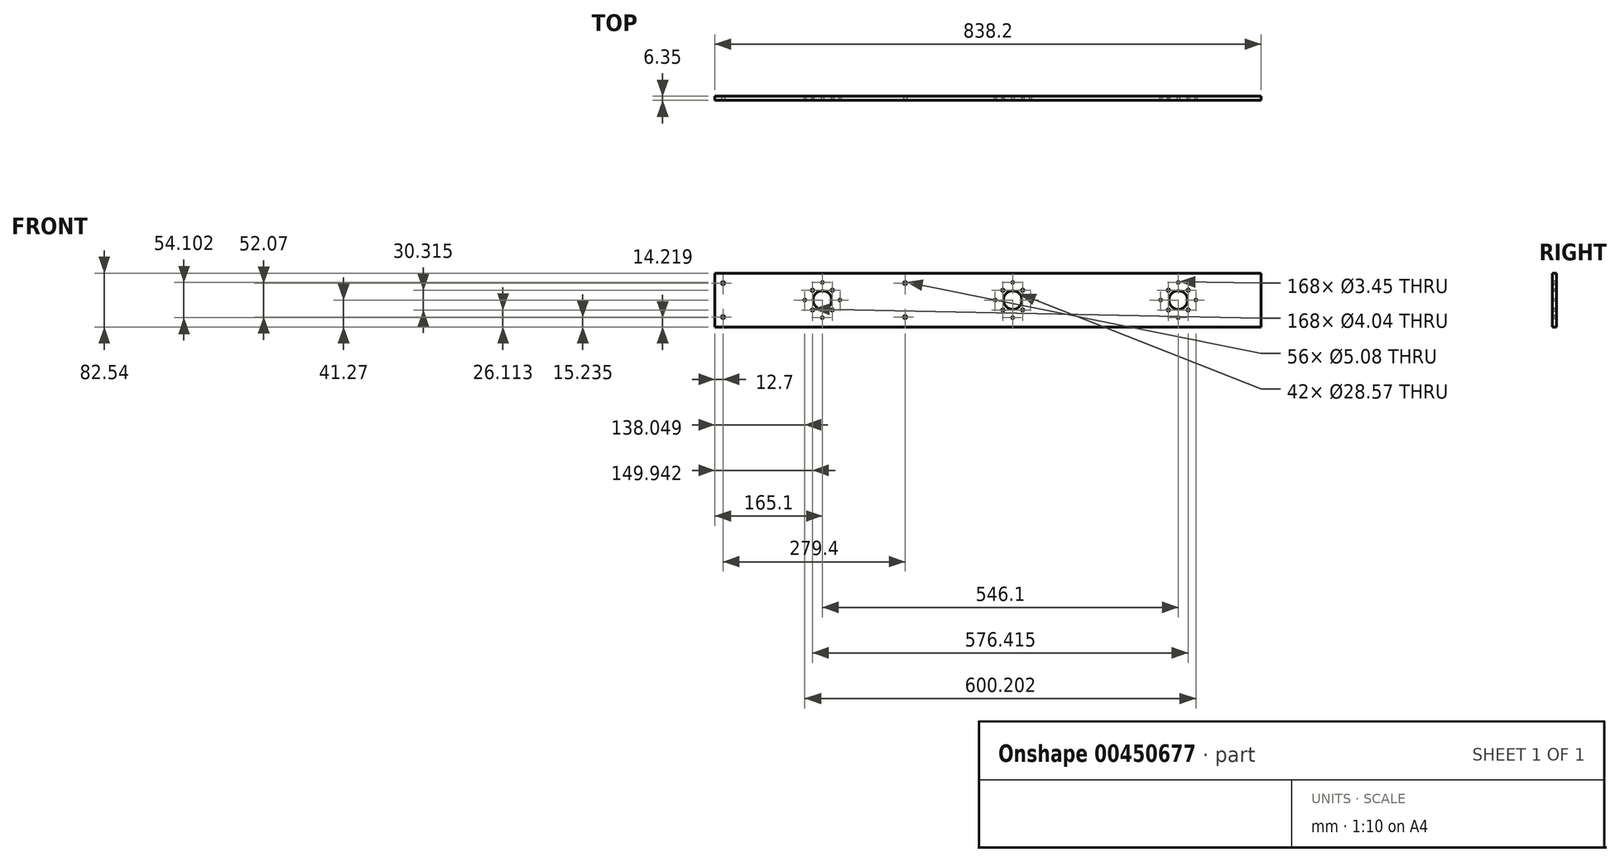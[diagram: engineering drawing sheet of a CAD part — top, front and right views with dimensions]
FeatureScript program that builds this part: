
annotation { "Feature Type Name" : "Feature", "Feature Type Description" : "" }
export const myFeature = defineFeature(function(context is Context, id is Id, definition is map)
    precondition{}
    {
        {
            var Q0;
            Q0=qCreatedBy(makeId("Front.planeOp"),FACE);
            var sketch = newSketch(context, id + "F0", { "sketchPlane" : qUnion([Q0])});
            skLineSegment(sketch, "E0.bottom", {"start": v(419.1, 41.28) * mm, "end": v(-419.1, 41.28) * mm});
            skLineSegment(sketch, "E0.top", {"start": v(419.1, -41.28) * mm, "end": v(-419.1, -41.28) * mm});
            skLineSegment(sketch, "E0.left", {"start": v(419.1, 41.28) * mm, "end": v(419.1, -41.28) * mm});
            skLineSegment(sketch, "E0.right", {"start": v(-419.1, 41.28) * mm, "end": v(-419.1, -41.28) * mm});
            skPoint(sketch, "E0.middle", {"position": v(0, 0) * mm});
            skSolve(sketch);
        }
        {
            var Q0;
            Q0=makeQuery(id+"F0.imprint","IMPRINT",FACE,{"disambiguationData":[TD([[makeQuery(id+"F0.imprint","IMPRINT",EDGE,{"derivedFrom":sQuery(id+"F0.wireOp",EDGE,"E0.bottom")}),1.0]])]});
            extrude(context, id + "F1", {"entities" : qUnion([Q0]), "depth" : 6.35 * mm});
        }
        {
            var Q0;
            Q0=makeQuery(id+"F1.opExtrude","CAP_FACE",FACE,{"disambiguationData":[OSD([sQuery(id+"F0.wireOp",EDGE,"E0.bottom"),sQuery(id+"F0.wireOp",EDGE,"E0.top"),sQuery(id+"F0.wireOp",EDGE,"E0.left"),sQuery(id+"F0.wireOp",EDGE,"E0.right")])],"isStart":false});
            var sketch = newSketch(context, id + "F2", { "sketchPlane" : qUnion([Q0])});
            skLineSegment(sketch, "E1", {"start": v(-419.1, 0) * mm, "end": v(-254, 0) * mm});
            skLineSegment(sketch, "E2", {"start": v(-254, 0) * mm, "end": v(-226.95, 0) * mm});
            skLineSegment(sketch, "E3", {"start": v(-254, 0) * mm, "end": v(-254, 27.05) * mm});
            skLineSegment(sketch, "E4", {"start": v(-254, 0) * mm, "end": v(-254, -27.05) * mm});
            skPoint(sketch, "E5", {"position": v(-281.05, 0) * mm});
            skCircle(sketch, "E6", {"center": v(-254, 27.05) * mm, "radius": 1.73 * mm});
            skCircle(sketch, "E7", {"center": v(-226.95, 0) * mm, "radius": 1.73 * mm});
            skCircle(sketch, "E8", {"center": v(-254, -27.05) * mm, "radius": 1.73 * mm});
            skCircle(sketch, "E9", {"center": v(-281.05, 0) * mm, "radius": 1.73 * mm});
            skCircle(sketch, "E10", {"center": v(-254, 0) * mm, "radius": 14.29 * mm});
            skLineSegment(sketch, "E11", {"start": v(419.1, 0) * mm, "end": v(292.1, 0) * mm});
            skPoint(sketch, "E11.endSnap0", {"position": v(419.1, 0) * mm});
            skPoint(sketch, "E12", {"position": v(319.15, 0) * mm});
            skLineSegment(sketch, "E13", {"start": v(292.1, 0) * mm, "end": v(292.1, 27.05) * mm});
            skLineSegment(sketch, "E14", {"start": v(292.1, 0) * mm, "end": v(292.1, -27.05) * mm});
            skLineSegment(sketch, "E15", {"start": v(292.1, 0) * mm, "end": v(265.05, 0) * mm});
            skCircle(sketch, "E16", {"center": v(292.1, 27.05) * mm, "radius": 1.73 * mm});
            skCircle(sketch, "E17", {"center": v(319.15, 0) * mm, "radius": 1.73 * mm});
            skCircle(sketch, "E18", {"center": v(292.1, -27.05) * mm, "radius": 1.73 * mm});
            skCircle(sketch, "E19", {"center": v(265.05, 0) * mm, "radius": 1.73 * mm});
            skCircle(sketch, "E20", {"center": v(292.1, 0) * mm, "radius": 14.29 * mm});
            skLineSegment(sketch, "E21", {"start": v(38.1, 0) * mm, "end": v(65.15, 0) * mm});
            skLineSegment(sketch, "E22", {"start": v(38.1, 0) * mm, "end": v(38.1, 27.05) * mm});
            skLineSegment(sketch, "E23", {"start": v(38.1, 0) * mm, "end": v(38.1, -27.05) * mm});
            skPoint(sketch, "E24", {"position": v(11.05, 0.16) * mm});
            skCircle(sketch, "E25", {"center": v(38.1, 27.05) * mm, "radius": 1.73 * mm});
            skCircle(sketch, "E26", {"center": v(65.15, 0) * mm, "radius": 1.73 * mm});
            skCircle(sketch, "E27", {"center": v(38.1, -27.05) * mm, "radius": 1.73 * mm});
            skCircle(sketch, "E28", {"center": v(11.05, 0.16) * mm, "radius": 1.73 * mm});
            skCircle(sketch, "E29", {"center": v(38.1, 0) * mm, "radius": 14.29 * mm});
            skLineSegment(sketch, "E30", {"start": v(292.1, 15.16) * mm, "end": v(307.26, 15.16) * mm});
            skLineSegment(sketch, "E31", {"start": v(307.26, 15.16) * mm, "end": v(307.26, -15.16) * mm});
            skLineSegment(sketch, "E32", {"start": v(307.26, -15.16) * mm, "end": v(276.94, -15.16) * mm});
            skLineSegment(sketch, "E33", {"start": v(276.94, -15.16) * mm, "end": v(276.94, 15.16) * mm});
            skLineSegment(sketch, "E34", {"start": v(276.94, 15.16) * mm, "end": v(307.26, 15.16) * mm});
            skCircle(sketch, "E35", {"center": v(276.94, 15.16) * mm, "radius": 2.02 * mm});
            skCircle(sketch, "E36", {"center": v(307.26, 15.16) * mm, "radius": 2.02 * mm});
            skCircle(sketch, "E37", {"center": v(307.26, -15.16) * mm, "radius": 2.02 * mm});
            skCircle(sketch, "E38", {"center": v(276.94, -15.16) * mm, "radius": 2.02 * mm});
            skLineSegment(sketch, "E39", {"start": v(53.26, 15.16) * mm, "end": v(53.26, -15.16) * mm});
            skLineSegment(sketch, "E40", {"start": v(53.26, -15.16) * mm, "end": v(22.94, -15.16) * mm});
            skLineSegment(sketch, "E41", {"start": v(22.94, -15.16) * mm, "end": v(22.94, 15.16) * mm});
            skLineSegment(sketch, "E42", {"start": v(22.94, 15.16) * mm, "end": v(53.26, 15.16) * mm});
            skCircle(sketch, "E43", {"center": v(22.94, 15.16) * mm, "radius": 2.02 * mm});
            skCircle(sketch, "E44", {"center": v(53.26, 15.16) * mm, "radius": 2.02 * mm});
            skCircle(sketch, "E45", {"center": v(53.26, -15.16) * mm, "radius": 2.02 * mm});
            skCircle(sketch, "E46", {"center": v(22.94, -15.16) * mm, "radius": 2.02 * mm});
            skLineSegment(sketch, "E47", {"start": v(53.26, 0) * mm, "end": v(22.94, 0) * mm});
            skLineSegment(sketch, "E48", {"start": v(-238.84, 15.16) * mm, "end": v(-238.84, -15.16) * mm});
            skLineSegment(sketch, "E49", {"start": v(-238.84, -15.16) * mm, "end": v(-269.16, -15.16) * mm});
            skLineSegment(sketch, "E50", {"start": v(-269.16, -15.16) * mm, "end": v(-269.16, 15.16) * mm});
            skLineSegment(sketch, "E51", {"start": v(-269.16, 15.16) * mm, "end": v(-238.84, 15.16) * mm});
            skCircle(sketch, "E52", {"center": v(-269.16, 15.16) * mm, "radius": 2.02 * mm});
            skCircle(sketch, "E53", {"center": v(-238.84, 15.16) * mm, "radius": 2.02 * mm});
            skCircle(sketch, "E54", {"center": v(-238.84, -15.16) * mm, "radius": 2.02 * mm});
            skCircle(sketch, "E55", {"center": v(-269.16, -15.16) * mm, "radius": 2.02 * mm});
            skLineSegment(sketch, "E56", {"start": v(-269.16, 0) * mm, "end": v(-238.84, 0) * mm});
            skLineSegment(sketch, "E57", {"start": v(0, 41.28) * mm, "end": v(38.1, 41.28) * mm});
            skLineSegment(sketch, "E58", {"start": v(38.1, 41.28) * mm, "end": v(38.1, -41.27) * mm});
            skSolve(sketch);
        }
        {
            var Q0;
            {var subQ1=sQuery(id+"F2.wireOp",EDGE,"E4");var subQ3=sQuery(id+"F2.wireOp",EDGE,"E10");var subQ4=makeQuery(id+"F2.imprint","INTERSECT",VERTEX,{"derivedFrom":[subQ1,subQ3]});Q0=makeQuery(id+"F2.imprint","IMPRINT",FACE,{"disambiguationData":[TD([[makeQuery(id+"F2.imprint","IMPRINT",EDGE,{"disambiguationData":[TD([[subQ4,-1.0]])],"derivedFrom":subQ3}),1.0]])]});}
            var Q1;
            {var subQ1=sQuery(id+"F2.wireOp",EDGE,"E3");var subQ3=sQuery(id+"F2.wireOp",EDGE,"E10");var subQ4=makeQuery(id+"F2.imprint","INTERSECT",VERTEX,{"derivedFrom":[subQ1,subQ3]});Q1=makeQuery(id+"F2.imprint","IMPRINT",FACE,{"disambiguationData":[TD([[makeQuery(id+"F2.imprint","IMPRINT",EDGE,{"disambiguationData":[TD([[subQ4,1.0]])],"derivedFrom":subQ3}),1.0]])]});}
            var Q2;
            {var subQ1=sQuery(id+"F2.wireOp",EDGE,"E3");var subQ3=sQuery(id+"F2.wireOp",EDGE,"E10");var subQ4=makeQuery(id+"F2.imprint","INTERSECT",VERTEX,{"derivedFrom":[subQ1,subQ3]});Q2=makeQuery(id+"F2.imprint","IMPRINT",FACE,{"disambiguationData":[TD([[makeQuery(id+"F2.imprint","IMPRINT",EDGE,{"disambiguationData":[TD([[subQ4,-1.0]])],"derivedFrom":subQ3}),1.0]])]});}
            var Q3;
            {var subQ1=sQuery(id+"F2.wireOp",EDGE,"E4");var subQ3=sQuery(id+"F2.wireOp",EDGE,"E10");var subQ4=makeQuery(id+"F2.imprint","INTERSECT",VERTEX,{"derivedFrom":[subQ1,subQ3]});Q3=makeQuery(id+"F2.imprint","IMPRINT",FACE,{"disambiguationData":[TD([[makeQuery(id+"F2.imprint","IMPRINT",EDGE,{"disambiguationData":[TD([[subQ4,1.0]])],"derivedFrom":subQ3}),1.0]])]});}
            var Q4;
            {var subQ0=sQuery(id+"F2.wireOp",EDGE,"E50");var subQ1=sQuery(id+"F2.wireOp",EDGE,"E49");var subQ2=makeQuery(id+"F2.imprint","INTERSECT",VERTEX,{"derivedFrom":[subQ1,subQ0]});Q4=makeQuery(id+"F2.imprint","IMPRINT",FACE,{"disambiguationData":[TD([[makeQuery(id+"F2.imprint","IMPRINT",EDGE,{"disambiguationData":[TD([[subQ2,1.0]])],"derivedFrom":subQ1}),1.0]])]});}
            var Q5;
            {var subQ0=sQuery(id+"F2.wireOp",EDGE,"E50");var subQ1=sQuery(id+"F2.wireOp",EDGE,"E49");var subQ2=makeQuery(id+"F2.imprint","INTERSECT",VERTEX,{"derivedFrom":[subQ1,subQ0]});Q5=makeQuery(id+"F2.imprint","IMPRINT",FACE,{"disambiguationData":[TD([[makeQuery(id+"F2.imprint","IMPRINT",EDGE,{"disambiguationData":[TD([[subQ2,1.0]])],"derivedFrom":subQ1}),-1.0]])]});}
            var Q6;
            Q6=makeQuery(id+"F2.imprint","IMPRINT",FACE,{"disambiguationData":[TD([[makeQuery(id+"F2.imprint","IMPRINT",EDGE,{"derivedFrom":sQuery(id+"F2.wireOp",EDGE,"E8")}),1.0]])]});
            var Q7;
            {var subQ0=sQuery(id+"F2.wireOp",EDGE,"E49");var subQ1=sQuery(id+"F2.wireOp",EDGE,"E48");var subQ2=makeQuery(id+"F2.imprint","INTERSECT",VERTEX,{"derivedFrom":[subQ1,subQ0]});Q7=makeQuery(id+"F2.imprint","IMPRINT",FACE,{"disambiguationData":[TD([[makeQuery(id+"F2.imprint","IMPRINT",EDGE,{"disambiguationData":[TD([[subQ2,1.0]])],"derivedFrom":subQ1}),1.0]])]});}
            var Q8;
            {var subQ0=sQuery(id+"F2.wireOp",EDGE,"E49");var subQ1=sQuery(id+"F2.wireOp",EDGE,"E48");var subQ2=makeQuery(id+"F2.imprint","INTERSECT",VERTEX,{"derivedFrom":[subQ1,subQ0]});Q8=makeQuery(id+"F2.imprint","IMPRINT",FACE,{"disambiguationData":[TD([[makeQuery(id+"F2.imprint","IMPRINT",EDGE,{"disambiguationData":[TD([[subQ2,1.0]])],"derivedFrom":subQ1}),-1.0]])]});}
            var Q9;
            {var subQ0=sQuery(id+"F2.wireOp",EDGE,"E51");var subQ1=sQuery(id+"F2.wireOp",EDGE,"E48");var subQ2=makeQuery(id+"F2.imprint","INTERSECT",VERTEX,{"derivedFrom":[subQ1,subQ0]});Q9=makeQuery(id+"F2.imprint","IMPRINT",FACE,{"disambiguationData":[TD([[makeQuery(id+"F2.imprint","IMPRINT",EDGE,{"disambiguationData":[TD([[subQ2,-1.0]])],"derivedFrom":subQ1}),1.0]])]});}
            var Q10;
            {var subQ0=sQuery(id+"F2.wireOp",EDGE,"E51");var subQ1=sQuery(id+"F2.wireOp",EDGE,"E48");var subQ2=makeQuery(id+"F2.imprint","INTERSECT",VERTEX,{"derivedFrom":[subQ1,subQ0]});Q10=makeQuery(id+"F2.imprint","IMPRINT",FACE,{"disambiguationData":[TD([[makeQuery(id+"F2.imprint","IMPRINT",EDGE,{"disambiguationData":[TD([[subQ2,-1.0]])],"derivedFrom":subQ1}),-1.0]])]});}
            var Q11;
            Q11=makeQuery(id+"F2.imprint","IMPRINT",FACE,{"disambiguationData":[TD([[makeQuery(id+"F2.imprint","IMPRINT",EDGE,{"derivedFrom":sQuery(id+"F2.wireOp",EDGE,"E7")}),1.0]])]});
            var Q12;
            Q12=makeQuery(id+"F2.imprint","IMPRINT",FACE,{"disambiguationData":[TD([[makeQuery(id+"F2.imprint","IMPRINT",EDGE,{"derivedFrom":sQuery(id+"F2.wireOp",EDGE,"E6")}),1.0]])]});
            var Q13;
            {var subQ0=sQuery(id+"F2.wireOp",EDGE,"E51");var subQ1=sQuery(id+"F2.wireOp",EDGE,"E50");var subQ2=makeQuery(id+"F2.imprint","INTERSECT",VERTEX,{"derivedFrom":[subQ1,subQ0]});Q13=makeQuery(id+"F2.imprint","IMPRINT",FACE,{"disambiguationData":[TD([[makeQuery(id+"F2.imprint","IMPRINT",EDGE,{"disambiguationData":[TD([[subQ2,1.0]])],"derivedFrom":subQ1}),-1.0]])]});}
            var Q14;
            {var subQ0=sQuery(id+"F2.wireOp",EDGE,"E51");var subQ1=sQuery(id+"F2.wireOp",EDGE,"E50");var subQ2=makeQuery(id+"F2.imprint","INTERSECT",VERTEX,{"derivedFrom":[subQ1,subQ0]});Q14=makeQuery(id+"F2.imprint","IMPRINT",FACE,{"disambiguationData":[TD([[makeQuery(id+"F2.imprint","IMPRINT",EDGE,{"disambiguationData":[TD([[subQ2,1.0]])],"derivedFrom":subQ1}),1.0]])]});}
            var Q15;
            {var subQ0=sQuery(id+"F2.wireOp",EDGE,"E9");var subQ1=sQuery(id+"F2.wireOp",EDGE,"E1");var subQ2=makeQuery(id+"F2.imprint","INTERSECT",VERTEX,{"disambiguationData":[OD(0.0)],"derivedFrom":[subQ1,subQ0]});Q15=makeQuery(id+"F2.imprint","IMPRINT",FACE,{"disambiguationData":[TD([[makeQuery(id+"F2.imprint","IMPRINT",EDGE,{"disambiguationData":[TD([[subQ2,-1.0]])],"derivedFrom":subQ1}),-1.0]])]});}
            var Q16;
            {var subQ0=sQuery(id+"F2.wireOp",EDGE,"E9");var subQ1=sQuery(id+"F2.wireOp",EDGE,"E1");var subQ2=makeQuery(id+"F2.imprint","INTERSECT",VERTEX,{"disambiguationData":[OD(0.0)],"derivedFrom":[subQ1,subQ0]});Q16=makeQuery(id+"F2.imprint","IMPRINT",FACE,{"disambiguationData":[TD([[makeQuery(id+"F2.imprint","IMPRINT",EDGE,{"disambiguationData":[TD([[subQ2,-1.0]])],"derivedFrom":subQ1}),1.0]])]});}
            var Q17;
            {var subQ1=sQuery(id+"F2.wireOp",EDGE,"E23");var subQ3=sQuery(id+"F2.wireOp",EDGE,"E29");var subQ4=makeQuery(id+"F2.imprint","INTERSECT",VERTEX,{"derivedFrom":[subQ1,subQ3]});Q17=makeQuery(id+"F2.imprint","IMPRINT",FACE,{"disambiguationData":[TD([[makeQuery(id+"F2.imprint","IMPRINT",EDGE,{"disambiguationData":[TD([[subQ4,-1.0]])],"derivedFrom":subQ3}),1.0]])]});}
            var Q18;
            {var subQ1=sQuery(id+"F2.wireOp",EDGE,"E23");var subQ3=sQuery(id+"F2.wireOp",EDGE,"E29");var subQ4=makeQuery(id+"F2.imprint","INTERSECT",VERTEX,{"derivedFrom":[subQ1,subQ3]});Q18=makeQuery(id+"F2.imprint","IMPRINT",FACE,{"disambiguationData":[TD([[makeQuery(id+"F2.imprint","IMPRINT",EDGE,{"disambiguationData":[TD([[subQ4,1.0]])],"derivedFrom":subQ3}),1.0]])]});}
            var Q19;
            {var subQ1=sQuery(id+"F2.wireOp",EDGE,"E22");var subQ3=sQuery(id+"F2.wireOp",EDGE,"E29");var subQ4=makeQuery(id+"F2.imprint","INTERSECT",VERTEX,{"derivedFrom":[subQ1,subQ3]});Q19=makeQuery(id+"F2.imprint","IMPRINT",FACE,{"disambiguationData":[TD([[makeQuery(id+"F2.imprint","IMPRINT",EDGE,{"disambiguationData":[TD([[subQ4,-1.0]])],"derivedFrom":subQ3}),1.0]])]});}
            var Q20;
            {var subQ1=sQuery(id+"F2.wireOp",EDGE,"E22");var subQ3=sQuery(id+"F2.wireOp",EDGE,"E29");var subQ4=makeQuery(id+"F2.imprint","INTERSECT",VERTEX,{"derivedFrom":[subQ1,subQ3]});Q20=makeQuery(id+"F2.imprint","IMPRINT",FACE,{"disambiguationData":[TD([[makeQuery(id+"F2.imprint","IMPRINT",EDGE,{"disambiguationData":[TD([[subQ4,1.0]])],"derivedFrom":subQ3}),1.0]])]});}
            var Q21;
            {var subQ0=sQuery(id+"F2.wireOp",EDGE,"E42");var subQ1=sQuery(id+"F2.wireOp",EDGE,"E39");var subQ2=makeQuery(id+"F2.imprint","INTERSECT",VERTEX,{"derivedFrom":[subQ1,subQ0]});Q21=makeQuery(id+"F2.imprint","IMPRINT",FACE,{"disambiguationData":[TD([[makeQuery(id+"F2.imprint","IMPRINT",EDGE,{"disambiguationData":[TD([[subQ2,-1.0]])],"derivedFrom":subQ1}),1.0]])]});}
            var Q22;
            {var subQ0=sQuery(id+"F2.wireOp",EDGE,"E42");var subQ1=sQuery(id+"F2.wireOp",EDGE,"E39");var subQ2=makeQuery(id+"F2.imprint","INTERSECT",VERTEX,{"derivedFrom":[subQ1,subQ0]});Q22=makeQuery(id+"F2.imprint","IMPRINT",FACE,{"disambiguationData":[TD([[makeQuery(id+"F2.imprint","IMPRINT",EDGE,{"disambiguationData":[TD([[subQ2,-1.0]])],"derivedFrom":subQ1}),-1.0]])]});}
            var Q23;
            Q23=makeQuery(id+"F2.imprint","IMPRINT",FACE,{"disambiguationData":[TD([[makeQuery(id+"F2.imprint","IMPRINT",EDGE,{"derivedFrom":sQuery(id+"F2.wireOp",EDGE,"E25")}),1.0]])]});
            var Q24;
            {var subQ0=sQuery(id+"F2.wireOp",EDGE,"E42");var subQ1=sQuery(id+"F2.wireOp",EDGE,"E41");var subQ2=makeQuery(id+"F2.imprint","INTERSECT",VERTEX,{"derivedFrom":[subQ1,subQ0]});Q24=makeQuery(id+"F2.imprint","IMPRINT",FACE,{"disambiguationData":[TD([[makeQuery(id+"F2.imprint","IMPRINT",EDGE,{"disambiguationData":[TD([[subQ2,1.0]])],"derivedFrom":subQ1}),1.0]])]});}
            var Q25;
            {var subQ0=sQuery(id+"F2.wireOp",EDGE,"E42");var subQ1=sQuery(id+"F2.wireOp",EDGE,"E41");var subQ2=makeQuery(id+"F2.imprint","INTERSECT",VERTEX,{"derivedFrom":[subQ1,subQ0]});Q25=makeQuery(id+"F2.imprint","IMPRINT",FACE,{"disambiguationData":[TD([[makeQuery(id+"F2.imprint","IMPRINT",EDGE,{"disambiguationData":[TD([[subQ2,1.0]])],"derivedFrom":subQ1}),-1.0]])]});}
            var Q26;
            {var subQ0=sQuery(id+"F2.wireOp",EDGE,"E41");var subQ1=sQuery(id+"F2.wireOp",EDGE,"E40");var subQ2=makeQuery(id+"F2.imprint","INTERSECT",VERTEX,{"derivedFrom":[subQ1,subQ0]});Q26=makeQuery(id+"F2.imprint","IMPRINT",FACE,{"disambiguationData":[TD([[makeQuery(id+"F2.imprint","IMPRINT",EDGE,{"disambiguationData":[TD([[subQ2,1.0]])],"derivedFrom":subQ1}),1.0]])]});}
            var Q27;
            {var subQ0=sQuery(id+"F2.wireOp",EDGE,"E41");var subQ1=sQuery(id+"F2.wireOp",EDGE,"E40");var subQ2=makeQuery(id+"F2.imprint","INTERSECT",VERTEX,{"derivedFrom":[subQ1,subQ0]});Q27=makeQuery(id+"F2.imprint","IMPRINT",FACE,{"disambiguationData":[TD([[makeQuery(id+"F2.imprint","IMPRINT",EDGE,{"disambiguationData":[TD([[subQ2,1.0]])],"derivedFrom":subQ1}),-1.0]])]});}
            var Q28;
            Q28=makeQuery(id+"F2.imprint","IMPRINT",FACE,{"disambiguationData":[TD([[makeQuery(id+"F2.imprint","IMPRINT",EDGE,{"derivedFrom":sQuery(id+"F2.wireOp",EDGE,"E27")}),1.0]])]});
            var Q29;
            {var subQ0=sQuery(id+"F2.wireOp",EDGE,"E40");var subQ1=sQuery(id+"F2.wireOp",EDGE,"E39");var subQ2=makeQuery(id+"F2.imprint","INTERSECT",VERTEX,{"derivedFrom":[subQ1,subQ0]});Q29=makeQuery(id+"F2.imprint","IMPRINT",FACE,{"disambiguationData":[TD([[makeQuery(id+"F2.imprint","IMPRINT",EDGE,{"disambiguationData":[TD([[subQ2,1.0]])],"derivedFrom":subQ1}),1.0]])]});}
            var Q30;
            {var subQ0=sQuery(id+"F2.wireOp",EDGE,"E40");var subQ1=sQuery(id+"F2.wireOp",EDGE,"E39");var subQ2=makeQuery(id+"F2.imprint","INTERSECT",VERTEX,{"derivedFrom":[subQ1,subQ0]});Q30=makeQuery(id+"F2.imprint","IMPRINT",FACE,{"disambiguationData":[TD([[makeQuery(id+"F2.imprint","IMPRINT",EDGE,{"disambiguationData":[TD([[subQ2,1.0]])],"derivedFrom":subQ1}),-1.0]])]});}
            var Q31;
            Q31=makeQuery(id+"F2.imprint","IMPRINT",FACE,{"disambiguationData":[TD([[makeQuery(id+"F2.imprint","IMPRINT",EDGE,{"derivedFrom":sQuery(id+"F2.wireOp",EDGE,"E28")}),1.0]])]});
            var Q32;
            Q32=makeQuery(id+"F2.imprint","IMPRINT",FACE,{"disambiguationData":[TD([[makeQuery(id+"F2.imprint","IMPRINT",EDGE,{"derivedFrom":sQuery(id+"F2.wireOp",EDGE,"E26")}),1.0]])]});
            var Q33;
            {var subQ1=sQuery(id+"F2.wireOp",EDGE,"E11");var subQ3=sQuery(id+"F2.wireOp",EDGE,"E20");var subQ4=makeQuery(id+"F2.imprint","INTERSECT",VERTEX,{"derivedFrom":[subQ1,subQ3]});Q33=makeQuery(id+"F2.imprint","IMPRINT",FACE,{"disambiguationData":[TD([[makeQuery(id+"F2.imprint","IMPRINT",EDGE,{"disambiguationData":[TD([[subQ4,1.0]])],"derivedFrom":subQ3}),1.0]])]});}
            var Q34;
            {var subQ1=sQuery(id+"F2.wireOp",EDGE,"E11");var subQ3=sQuery(id+"F2.wireOp",EDGE,"E20");var subQ4=makeQuery(id+"F2.imprint","INTERSECT",VERTEX,{"derivedFrom":[subQ1,subQ3]});Q34=makeQuery(id+"F2.imprint","IMPRINT",FACE,{"disambiguationData":[TD([[makeQuery(id+"F2.imprint","IMPRINT",EDGE,{"disambiguationData":[TD([[subQ4,-1.0]])],"derivedFrom":subQ3}),1.0]])]});}
            var Q35;
            {var subQ1=sQuery(id+"F2.wireOp",EDGE,"E13");var subQ3=sQuery(id+"F2.wireOp",EDGE,"E20");var subQ4=makeQuery(id+"F2.imprint","INTERSECT",VERTEX,{"derivedFrom":[subQ1,subQ3]});Q35=makeQuery(id+"F2.imprint","IMPRINT",FACE,{"disambiguationData":[TD([[makeQuery(id+"F2.imprint","IMPRINT",EDGE,{"disambiguationData":[TD([[subQ4,-1.0]])],"derivedFrom":subQ3}),1.0]])]});}
            var Q36;
            {var subQ1=sQuery(id+"F2.wireOp",EDGE,"E14");var subQ3=sQuery(id+"F2.wireOp",EDGE,"E20");var subQ4=makeQuery(id+"F2.imprint","INTERSECT",VERTEX,{"derivedFrom":[subQ1,subQ3]});Q36=makeQuery(id+"F2.imprint","IMPRINT",FACE,{"disambiguationData":[TD([[makeQuery(id+"F2.imprint","IMPRINT",EDGE,{"disambiguationData":[TD([[subQ4,1.0]])],"derivedFrom":subQ3}),1.0]])]});}
            var Q37;
            {var subQ0=sQuery(id+"F2.wireOp",EDGE,"E32");var subQ1=sQuery(id+"F2.wireOp",EDGE,"E31");var subQ2=makeQuery(id+"F2.imprint","INTERSECT",VERTEX,{"derivedFrom":[subQ1,subQ0]});Q37=makeQuery(id+"F2.imprint","IMPRINT",FACE,{"disambiguationData":[TD([[makeQuery(id+"F2.imprint","IMPRINT",EDGE,{"disambiguationData":[TD([[subQ2,1.0]])],"derivedFrom":subQ1}),1.0]])]});}
            var Q38;
            {var subQ0=sQuery(id+"F2.wireOp",EDGE,"E32");var subQ1=sQuery(id+"F2.wireOp",EDGE,"E31");var subQ2=makeQuery(id+"F2.imprint","INTERSECT",VERTEX,{"derivedFrom":[subQ1,subQ0]});Q38=makeQuery(id+"F2.imprint","IMPRINT",FACE,{"disambiguationData":[TD([[makeQuery(id+"F2.imprint","IMPRINT",EDGE,{"disambiguationData":[TD([[subQ2,1.0]])],"derivedFrom":subQ1}),-1.0]])]});}
            var Q39;
            Q39=makeQuery(id+"F2.imprint","IMPRINT",FACE,{"disambiguationData":[TD([[makeQuery(id+"F2.imprint","IMPRINT",EDGE,{"derivedFrom":sQuery(id+"F2.wireOp",EDGE,"E18")}),1.0]])]});
            var Q40;
            {var subQ0=sQuery(id+"F2.wireOp",EDGE,"E17");var subQ1=sQuery(id+"F2.wireOp",EDGE,"E11");var subQ2=makeQuery(id+"F2.imprint","INTERSECT",VERTEX,{"disambiguationData":[OD(0.0)],"derivedFrom":[subQ1,subQ0]});Q40=makeQuery(id+"F2.imprint","IMPRINT",FACE,{"disambiguationData":[TD([[makeQuery(id+"F2.imprint","IMPRINT",EDGE,{"disambiguationData":[TD([[subQ2,1.0]])],"derivedFrom":subQ1}),1.0]])]});}
            var Q41;
            {var subQ0=sQuery(id+"F2.wireOp",EDGE,"E17");var subQ1=sQuery(id+"F2.wireOp",EDGE,"E11");var subQ2=makeQuery(id+"F2.imprint","INTERSECT",VERTEX,{"disambiguationData":[OD(0.0)],"derivedFrom":[subQ1,subQ0]});Q41=makeQuery(id+"F2.imprint","IMPRINT",FACE,{"disambiguationData":[TD([[makeQuery(id+"F2.imprint","IMPRINT",EDGE,{"disambiguationData":[TD([[subQ2,1.0]])],"derivedFrom":subQ1}),-1.0]])]});}
            var Q42;
            {var subQ0=sQuery(id+"F2.wireOp",EDGE,"E34");var subQ1=sQuery(id+"F2.wireOp",EDGE,"E31");var subQ2=makeQuery(id+"F2.imprint","INTERSECT",VERTEX,{"derivedFrom":[subQ1,subQ0]});Q42=makeQuery(id+"F2.imprint","IMPRINT",FACE,{"disambiguationData":[TD([[makeQuery(id+"F2.imprint","IMPRINT",EDGE,{"disambiguationData":[TD([[subQ2,-1.0]])],"derivedFrom":subQ1}),1.0]])]});}
            var Q43;
            {var subQ0=sQuery(id+"F2.wireOp",EDGE,"E34");var subQ1=sQuery(id+"F2.wireOp",EDGE,"E31");var subQ2=makeQuery(id+"F2.imprint","INTERSECT",VERTEX,{"derivedFrom":[subQ1,subQ0]});Q43=makeQuery(id+"F2.imprint","IMPRINT",FACE,{"disambiguationData":[TD([[makeQuery(id+"F2.imprint","IMPRINT",EDGE,{"disambiguationData":[TD([[subQ2,-1.0]])],"derivedFrom":subQ1}),-1.0]])]});}
            var Q44;
            Q44=makeQuery(id+"F2.imprint","IMPRINT",FACE,{"disambiguationData":[TD([[makeQuery(id+"F2.imprint","IMPRINT",EDGE,{"derivedFrom":sQuery(id+"F2.wireOp",EDGE,"E16")}),1.0]])]});
            var Q45;
            {var subQ0=sQuery(id+"F2.wireOp",EDGE,"E34");var subQ1=sQuery(id+"F2.wireOp",EDGE,"E33");var subQ2=makeQuery(id+"F2.imprint","INTERSECT",VERTEX,{"derivedFrom":[subQ1,subQ0]});Q45=makeQuery(id+"F2.imprint","IMPRINT",FACE,{"disambiguationData":[TD([[makeQuery(id+"F2.imprint","IMPRINT",EDGE,{"disambiguationData":[TD([[subQ2,1.0]])],"derivedFrom":subQ1}),-1.0]])]});}
            var Q46;
            {var subQ0=sQuery(id+"F2.wireOp",EDGE,"E34");var subQ1=sQuery(id+"F2.wireOp",EDGE,"E33");var subQ2=makeQuery(id+"F2.imprint","INTERSECT",VERTEX,{"derivedFrom":[subQ1,subQ0]});Q46=makeQuery(id+"F2.imprint","IMPRINT",FACE,{"disambiguationData":[TD([[makeQuery(id+"F2.imprint","IMPRINT",EDGE,{"disambiguationData":[TD([[subQ2,1.0]])],"derivedFrom":subQ1}),1.0]])]});}
            var Q47;
            {var subQ0=sQuery(id+"F2.wireOp",EDGE,"E33");var subQ1=sQuery(id+"F2.wireOp",EDGE,"E32");var subQ2=makeQuery(id+"F2.imprint","INTERSECT",VERTEX,{"derivedFrom":[subQ1,subQ0]});Q47=makeQuery(id+"F2.imprint","IMPRINT",FACE,{"disambiguationData":[TD([[makeQuery(id+"F2.imprint","IMPRINT",EDGE,{"disambiguationData":[TD([[subQ2,1.0]])],"derivedFrom":subQ1}),1.0]])]});}
            var Q48;
            {var subQ0=sQuery(id+"F2.wireOp",EDGE,"E33");var subQ1=sQuery(id+"F2.wireOp",EDGE,"E32");var subQ2=makeQuery(id+"F2.imprint","INTERSECT",VERTEX,{"derivedFrom":[subQ1,subQ0]});Q48=makeQuery(id+"F2.imprint","IMPRINT",FACE,{"disambiguationData":[TD([[makeQuery(id+"F2.imprint","IMPRINT",EDGE,{"disambiguationData":[TD([[subQ2,1.0]])],"derivedFrom":subQ1}),-1.0]])]});}
            var Q49;
            Q49=makeQuery(id+"F2.imprint","IMPRINT",FACE,{"disambiguationData":[TD([[makeQuery(id+"F2.imprint","IMPRINT",EDGE,{"derivedFrom":sQuery(id+"F2.wireOp",EDGE,"E19")}),1.0]])]});
            var Q50;
            Q50=makeQuery(id+"F1.opExtrude","CAP_FACE",FACE,{"disambiguationData":[OSD([sQuery(id+"F0.wireOp",EDGE,"E0.bottom"),sQuery(id+"F0.wireOp",EDGE,"E0.top"),sQuery(id+"F0.wireOp",EDGE,"E0.left"),sQuery(id+"F0.wireOp",EDGE,"E0.right")])],"isStart":true});
            extrude(context, id + "F3", {"entities" : qUnion([Q0, Q1, Q2, Q3, Q4, Q5, Q6, Q7, Q8, Q9, Q10, Q11, Q12, Q13, Q14, Q15, Q16, Q17, Q18, Q19, Q20, Q21, Q22, Q23, Q24, Q25, Q26, Q27, Q28, Q29, Q30, Q31, Q32, Q33, Q34, Q35, Q36, Q37, Q38, Q39, Q40, Q41, Q42, Q43, Q44, Q45, Q46, Q47, Q48, Q49]), "operationType" : NewBodyOperationType.REMOVE, "endBound" : BoundingType.UP_TO_SURFACE, "oppositeDirection" : true, "endBoundEntityFace" : qUnion([Q50]), "depth" : 25.4 * mm});
        }
        {
            var Q0;
            Q0=makeQuery(id+"F1.opExtrude","CAP_FACE",FACE,{"disambiguationData":[OSD([sQuery(id+"F0.wireOp",EDGE,"E0.bottom"),sQuery(id+"F0.wireOp",EDGE,"E0.top"),sQuery(id+"F0.wireOp",EDGE,"E0.left"),sQuery(id+"F0.wireOp",EDGE,"E0.right")])],"isStart":false});
            var sketch = newSketch(context, id + "F4", { "sketchPlane" : qUnion([Q0])});
            skLineSegment(sketch, "E59", {"start": v(-406.4, 41.28) * mm, "end": v(-406.4, -41.28) * mm});
            skCircle(sketch, "E60", {"center": v(-406.4, -26.04) * mm, "radius": 2.54 * mm});
            skCircle(sketch, "E61", {"center": v(-406.4, 26.04) * mm, "radius": 2.54 * mm});
            skLineSegment(sketch, "E62", {"start": v(-254, 0) * mm, "end": v(-254, 41.27) * mm});
            skLineSegment(sketch, "E63", {"start": v(-254, 41.28) * mm, "end": v(0, 41.28) * mm});
            skLineSegment(sketch, "E64", {"start": v(-127, 41.28) * mm, "end": v(-127, -41.28) * mm});
            skCircle(sketch, "E65", {"center": v(-127, 26.04) * mm, "radius": 2.54 * mm});
            skCircle(sketch, "E66", {"center": v(-127, -26.04) * mm, "radius": 2.54 * mm});
            skSolve(sketch);
        }
        {
            var Q0;
            Q0=qSketchRegion(id+"F4",true);
            var Q1;
            Q1=makeQuery(id+"F1.opExtrude","CAP_FACE",FACE,{"disambiguationData":[OSD([sQuery(id+"F0.wireOp",EDGE,"E0.bottom"),sQuery(id+"F0.wireOp",EDGE,"E0.top"),sQuery(id+"F0.wireOp",EDGE,"E0.left"),sQuery(id+"F0.wireOp",EDGE,"E0.right")])],"isStart":true});
            extrude(context, id + "F5", {"entities" : qUnion([Q0]), "operationType" : NewBodyOperationType.REMOVE, "endBound" : BoundingType.UP_TO_SURFACE, "oppositeDirection" : true, "endBoundEntityFace" : qUnion([Q1]), "depth" : 25.4 * mm});
        }
    });
